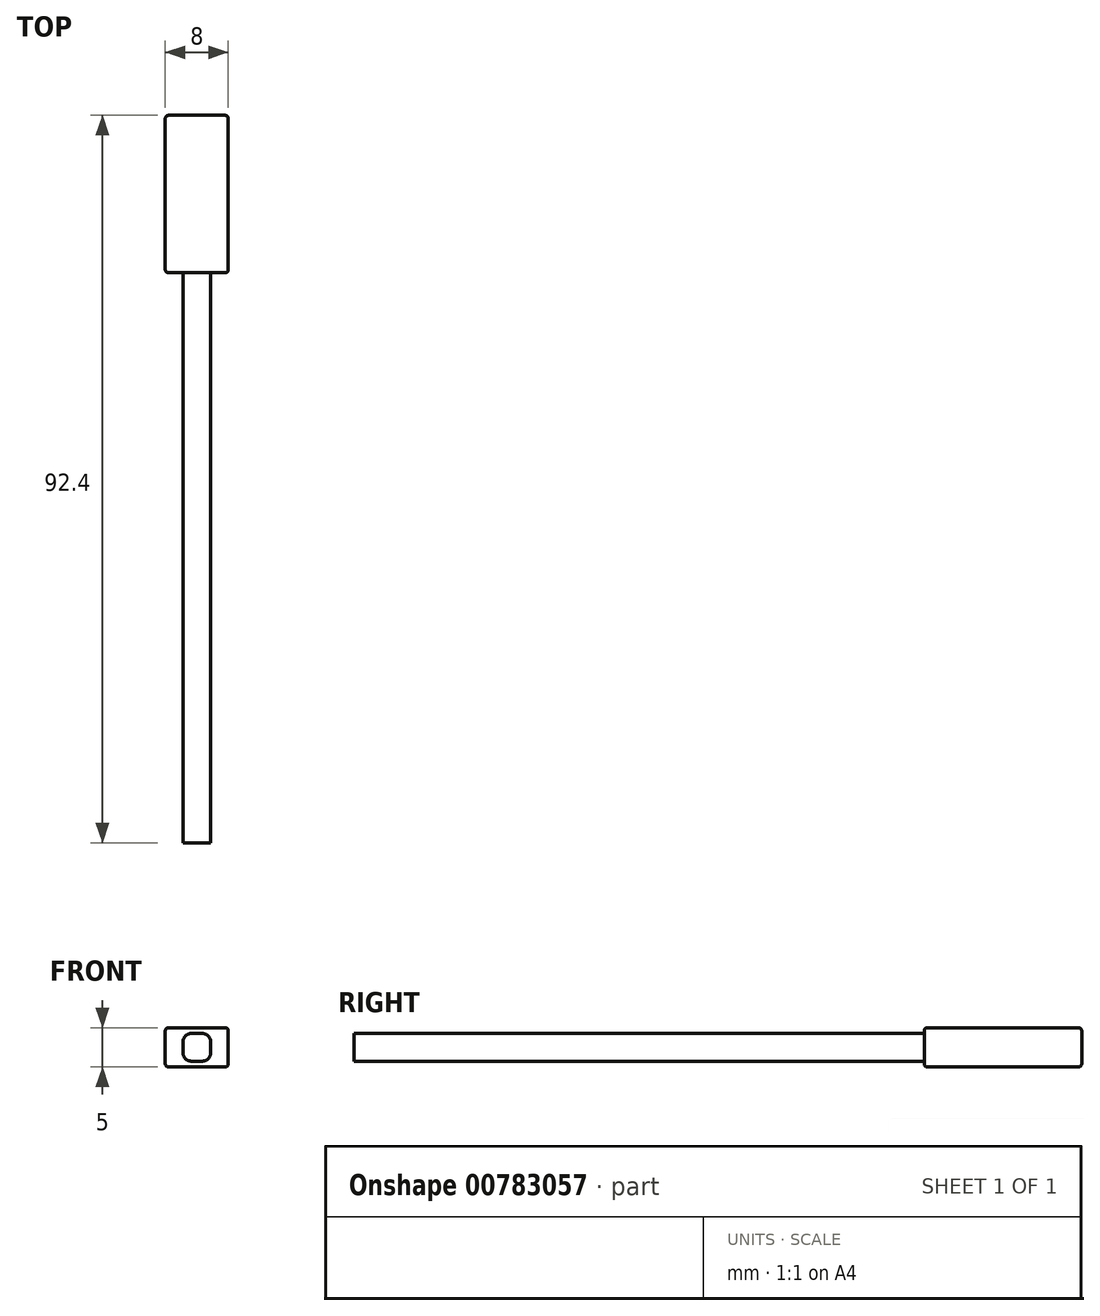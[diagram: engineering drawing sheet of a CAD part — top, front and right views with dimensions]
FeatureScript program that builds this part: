
annotation { "Feature Type Name" : "Feature", "Feature Type Description" : "" }
export const myFeature = defineFeature(function(context is Context, id is Id, definition is map)
    precondition{}
    {
        {
            var Q0;
            Q0=qCreatedBy(makeId("Top.planeOp"),FACE);
            var sketch = newSketch(context, id + "F0", { "sketchPlane" : qUnion([Q0])});
            skLineSegment(sketch, "E0.bottom", {"start": v(4, 10) * mm, "end": v(-4, 10) * mm});
            skLineSegment(sketch, "E0.top", {"start": v(4, -10) * mm, "end": v(-4, -10) * mm});
            skLineSegment(sketch, "E0.left", {"start": v(4, 10) * mm, "end": v(4, -10) * mm});
            skLineSegment(sketch, "E0.right", {"start": v(-4, 10) * mm, "end": v(-4, -10) * mm});
            skPoint(sketch, "E0.middle", {"position": v(0, 0) * mm});
            skSolve(sketch);
        }
        {
            var Q0;
            Q0 = qSketchRegion(id + "F0", true);
            extrude(context, id + "F1", {"entities" : qUnion([Q0]), "endBound" : BoundingType.SYMMETRIC, "depth" : 5 * mm, "offsetDistance" : 25 * mm});
        }
        {
            var Q0;
            Q0=qCreatedBy(makeId("Top.planeOp"),FACE);
            var sketch = newSketch(context, id + "F2", { "sketchPlane" : qUnion([Q0])});
            skLineSegment(sketch, "E1.bottom", {"start": v(-1.75, -7.4) * mm, "end": v(1.75, -7.4) * mm});
            skLineSegment(sketch, "E1.top", {"start": v(-1.75, -82.4) * mm, "end": v(1.75, -82.4) * mm});
            skLineSegment(sketch, "E1.left", {"start": v(-1.75, -7.4) * mm, "end": v(-1.75, -82.4) * mm});
            skLineSegment(sketch, "E1.right", {"start": v(1.75, -7.4) * mm, "end": v(1.75, -82.4) * mm});
            skPoint(sketch, "E1.middle", {"position": v(0, -44.9) * mm});
            skSolve(sketch);
        }
        {
            var Q0;
            Q0=makeQuery(id+"F2.imprint","IMPRINT",FACE,{"disambiguationData":[TD([[makeQuery(id+"F2.imprint","IMPRINT",EDGE,{"derivedFrom":sQuery(id+"F2.wireOp",EDGE,"E1.bottom")}),-1.0]])]});
            extrude(context, id + "F3", {"entities" : qUnion([Q0]), "operationType" : NewBodyOperationType.ADD, "endBound" : BoundingType.SYMMETRIC, "depth" : 3.5 * mm, "offsetDistance" : 25 * mm});
        }
        {
            var Q0;
            Q0=makeQuery(id+"F1.opExtrude","SWEPT_EDGE",EDGE,{"disambiguationData":[OSD([sQuery(id+"F0.wireOp",EDGE,"E0.bottom"),sQuery(id+"F0.wireOp",EDGE,"E0.left")])]});
            var Q1;
            Q1=makeQuery(id+"F1.opExtrude","CAP_EDGE",EDGE,{"disambiguationData":[OSD([sQuery(id+"F0.wireOp",EDGE,"E0.bottom")])],"isStart":true});
            var Q2;
            Q2=makeQuery(id+"F1.opExtrude","CAP_EDGE",EDGE,{"disambiguationData":[OSD([sQuery(id+"F0.wireOp",EDGE,"E0.bottom")])],"isStart":false});
            var Q3;
            Q3=makeQuery(id+"F1.opExtrude","CAP_EDGE",EDGE,{"disambiguationData":[OSD([sQuery(id+"F0.wireOp",EDGE,"E0.right")])],"isStart":false});
            var Q4;
            Q4=makeQuery(id+"F1.opExtrude","CAP_EDGE",EDGE,{"disambiguationData":[OSD([sQuery(id+"F0.wireOp",EDGE,"E0.left")])],"isStart":true});
            var Q5;
            Q5=makeQuery(id+"F1.opExtrude","CAP_EDGE",EDGE,{"disambiguationData":[OSD([sQuery(id+"F0.wireOp",EDGE,"E0.right")])],"isStart":true});
            var Q6;
            Q6=makeQuery(id+"F1.opExtrude","CAP_EDGE",EDGE,{"disambiguationData":[OSD([sQuery(id+"F0.wireOp",EDGE,"E0.left")])],"isStart":false});
            var Q7;
            Q7=makeQuery(id+"F1.opExtrude","SWEPT_EDGE",EDGE,{"disambiguationData":[OSD([sQuery(id+"F0.wireOp",EDGE,"E0.bottom"),sQuery(id+"F0.wireOp",EDGE,"E0.right")])]});
            var Q8;
            Q8=makeQuery(id+"F1.opExtrude","SWEPT_EDGE",EDGE,{"disambiguationData":[OSD([sQuery(id+"F0.wireOp",EDGE,"E0.top"),sQuery(id+"F0.wireOp",EDGE,"E0.left")])]});
            var Q9;
            Q9=makeQuery(id+"F1.opExtrude","CAP_EDGE",EDGE,{"disambiguationData":[OSD([sQuery(id+"F0.wireOp",EDGE,"E0.top")])],"isStart":false});
            var Q10;
            Q10=makeQuery(id+"F1.opExtrude","SWEPT_EDGE",EDGE,{"disambiguationData":[OSD([sQuery(id+"F0.wireOp",EDGE,"E0.top"),sQuery(id+"F0.wireOp",EDGE,"E0.right")])]});
            var Q11;
            Q11=makeQuery(id+"F1.opExtrude","CAP_EDGE",EDGE,{"disambiguationData":[OSD([sQuery(id+"F0.wireOp",EDGE,"E0.top")])],"isStart":true});
            fillet(context, id + "F4", {"entities" : qUnion([Q0, Q1, Q2, Q3, Q4, Q5, Q6, Q7, Q8, Q9, Q10, Q11]), "radius" : .4 * mm, "tangentPropagation" : true, "allowEdgeOverflow" : false});
        }
        {
            var Q0;
            Q0=makeQuery(id+"F3.opExtrude","CAP_EDGE",EDGE,{"disambiguationData":[OSD([sQuery(id+"F2.wireOp",EDGE,"E1.right")])],"isStart":true});
            var Q1;
            Q1=makeQuery(id+"F3.opExtrude","CAP_EDGE",EDGE,{"disambiguationData":[OSD([sQuery(id+"F2.wireOp",EDGE,"E1.left")])],"isStart":true});
            var Q2;
            Q2=makeQuery(id+"F3.opExtrude","CAP_EDGE",EDGE,{"disambiguationData":[OSD([sQuery(id+"F2.wireOp",EDGE,"E1.right")])],"isStart":false});
            var Q3;
            Q3=makeQuery(id+"F3.opExtrude","CAP_EDGE",EDGE,{"disambiguationData":[OSD([sQuery(id+"F2.wireOp",EDGE,"E1.left")])],"isStart":false});
            fillet(context, id + "F5", {"entities" : qUnion([Q0, Q1, Q2, Q3]), "radius" : 1 * mm, "tangentPropagation" : true, "allowEdgeOverflow" : false});
        }
    });
